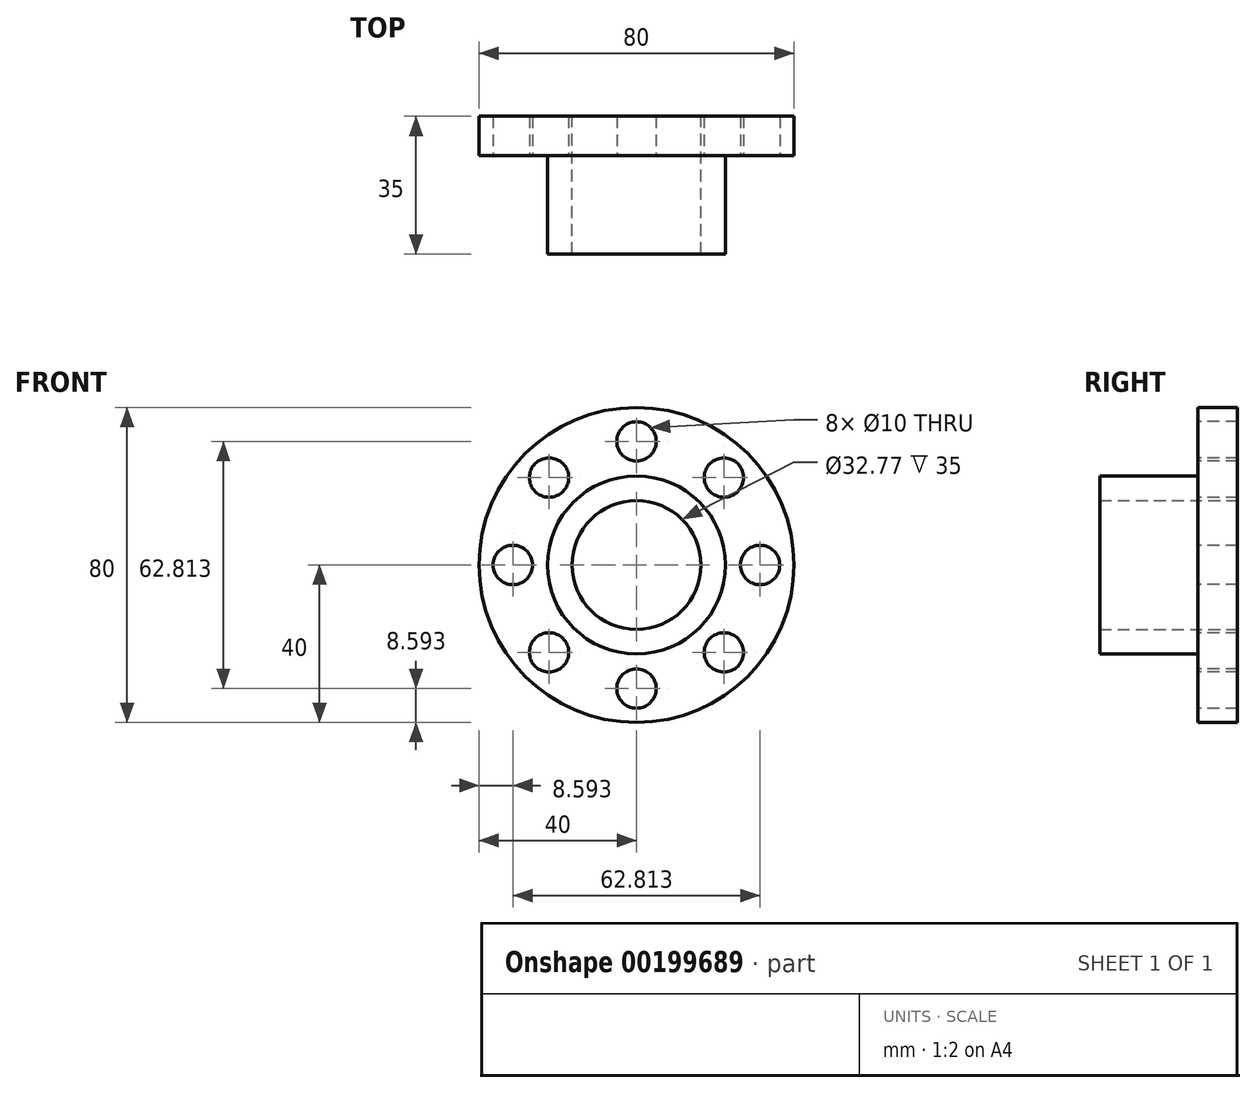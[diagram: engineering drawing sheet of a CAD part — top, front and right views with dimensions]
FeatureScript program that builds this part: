
annotation { "Feature Type Name" : "Feature", "Feature Type Description" : "" }
export const myFeature = defineFeature(function(context is Context, id is Id, definition is map)
    precondition{}
    {
        {
            var Q0;
            Q0=qCreatedBy(makeId("Front.planeOp"),FACE);
            var sketch = newSketch(context, id + "F0", { "sketchPlane" : qUnion([Q0])});
            skPoint(sketch, "E0.middle", {"position": v(0, 0) * mm});
            skCircle(sketch, "E1", {"center": v(0, 0) * mm, "radius": 40 * mm});
            skSolve(sketch);
        }
        {
            var Q0;
            Q0 = qSketchRegion(id + "F0", true);
            extrude(context, id + "F1", {"entities" : qUnion([Q0]), "depth" : 10 * mm});
        }
        {
            var Q0;
            Q0=makeQuery(id+"F1.opExtrude","CAP_FACE",FACE,{"disambiguationData":[OSD([sQuery(id+"F0.wireOp",EDGE,"E1")])],"isStart":false});
            var sketch = newSketch(context, id + "F2", { "sketchPlane" : qUnion([Q0])});
            skCircle(sketch, "E2", {"center": v(0, 0) * mm, "radius": 22.6 * mm});
            skCircle(sketch, "E3", {"center": v(0, 0) * mm, "radius": 16.39 * mm});
            skSolve(sketch);
        }
        {
            var Q0;
            Q0 = qSketchRegion(id + "F2", true);
            extrude(context, id + "F3", {"entities" : qUnion([Q0]), "operationType" : NewBodyOperationType.ADD, "depth" : 25 * mm});
        }
        {
            var Q0;
            Q0=makeQuery(id+"F3.boolean.opBoolean","SPLIT",FACE,{"disambiguationData":[TD([makeQuery(id+"F3.opExtrude","SWEPT_FACE",FACE,{"disambiguationData":[OSD([sQuery(id+"F2.wireOp",EDGE,"E3")])]})])],"derivedFrom":makeQuery(id+"F1.opExtrude","CAP_FACE",FACE,{"disambiguationData":[OSD([sQuery(id+"F0.wireOp",EDGE,"E1")])],"isStart":false})});
            extrude(context, id + "F4", {"entities" : qUnion([Q0]), "operationType" : NewBodyOperationType.REMOVE, "oppositeDirection" : true, "depth" : 25 * mm});
        }
        {
            var Q0;
            {var subQ0=sQuery(id+"F0.wireOp",EDGE,"E1");Q0=makeQuery(id+"F3.boolean.opBoolean","SPLIT",FACE,{"disambiguationData":[TD([makeQuery(id+"F1.opExtrude","SWEPT_FACE",FACE,{"disambiguationData":[OSD([subQ0])]})])],"derivedFrom":makeQuery(id+"F1.opExtrude","CAP_FACE",FACE,{"disambiguationData":[OSD([subQ0])],"isStart":false})});}
            var sketch = newSketch(context, id + "F5", { "sketchPlane" : qUnion([Q0])});
            skCircle(sketch, "E4", {"center": v(0, 31.4) * mm, "radius": 5 * mm});
            skCircle(sketch, "E5.1.0", {"center": v(-22.2, 22.2) * mm, "radius": 5 * mm});
            skCircle(sketch, "E5.2.0", {"center": v(-31.4, 0) * mm, "radius": 5 * mm});
            skCircle(sketch, "E5.3.0", {"center": v(-22.2, -22.2) * mm, "radius": 5 * mm});
            skCircle(sketch, "E5.4.0", {"center": v(0, -31.4) * mm, "radius": 5 * mm});
            skCircle(sketch, "E5.5.0", {"center": v(22.2, -22.2) * mm, "radius": 5 * mm});
            skCircle(sketch, "E5.6.0", {"center": v(31.4, 0) * mm, "radius": 5 * mm});
            skCircle(sketch, "E5.7.0", {"center": v(22.2, 22.2) * mm, "radius": 5 * mm});
            skPoint(sketch, "E5.center", {"position": v(0, 0) * mm});
            skSolve(sketch);
        }
        {
            var Q0;
            Q0 = qSketchRegion(id + "F5", true);
            extrude(context, id + "F6", {"entities" : qUnion([Q0]), "operationType" : NewBodyOperationType.REMOVE, "oppositeDirection" : true, "depth" : 25 * mm});
        }
    });
